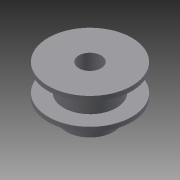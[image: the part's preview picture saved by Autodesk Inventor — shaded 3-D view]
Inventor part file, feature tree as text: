
AUTODESK INVENTOR PART (.ipt)
format: ipt  version: 2015 (Build 190159000, 159)  size: 116,224 bytes
history: native  units: mm
features: sketch x2, revolve x1, hole x1
ambient origin geometry x8: Origin, YZ Plane, XZ Plane, XY Plane, X Axis, Y Axis, Z Axis, Center Point
bodies: Solid1 (feature_tree)
feature tree (4):
  revolve  "Revolution1"  [1 undecoded]
  hole  "Hole1"  [1 undecoded]
  sketch  "Sketch1"  dims[d0=30.0mm d1=17.5mm]
  sketch  "Sketch2"  dims[d2=8.0mm d3=11.2mm d4=8.0mm d5=17.0mm d6=18.89mm d7=90.0deg d8=3.0mm d9=2.459mm d10=6.0mm d11=4.0mm d12=2.0mm d13=90.0deg d14=8.0mm d15=20.594885mm]
note: 2 required parameter values undecoded (feature->parameter linkage not recoverable at this tier; creation-order binding heuristic only, values carry confidence <= 0.55)